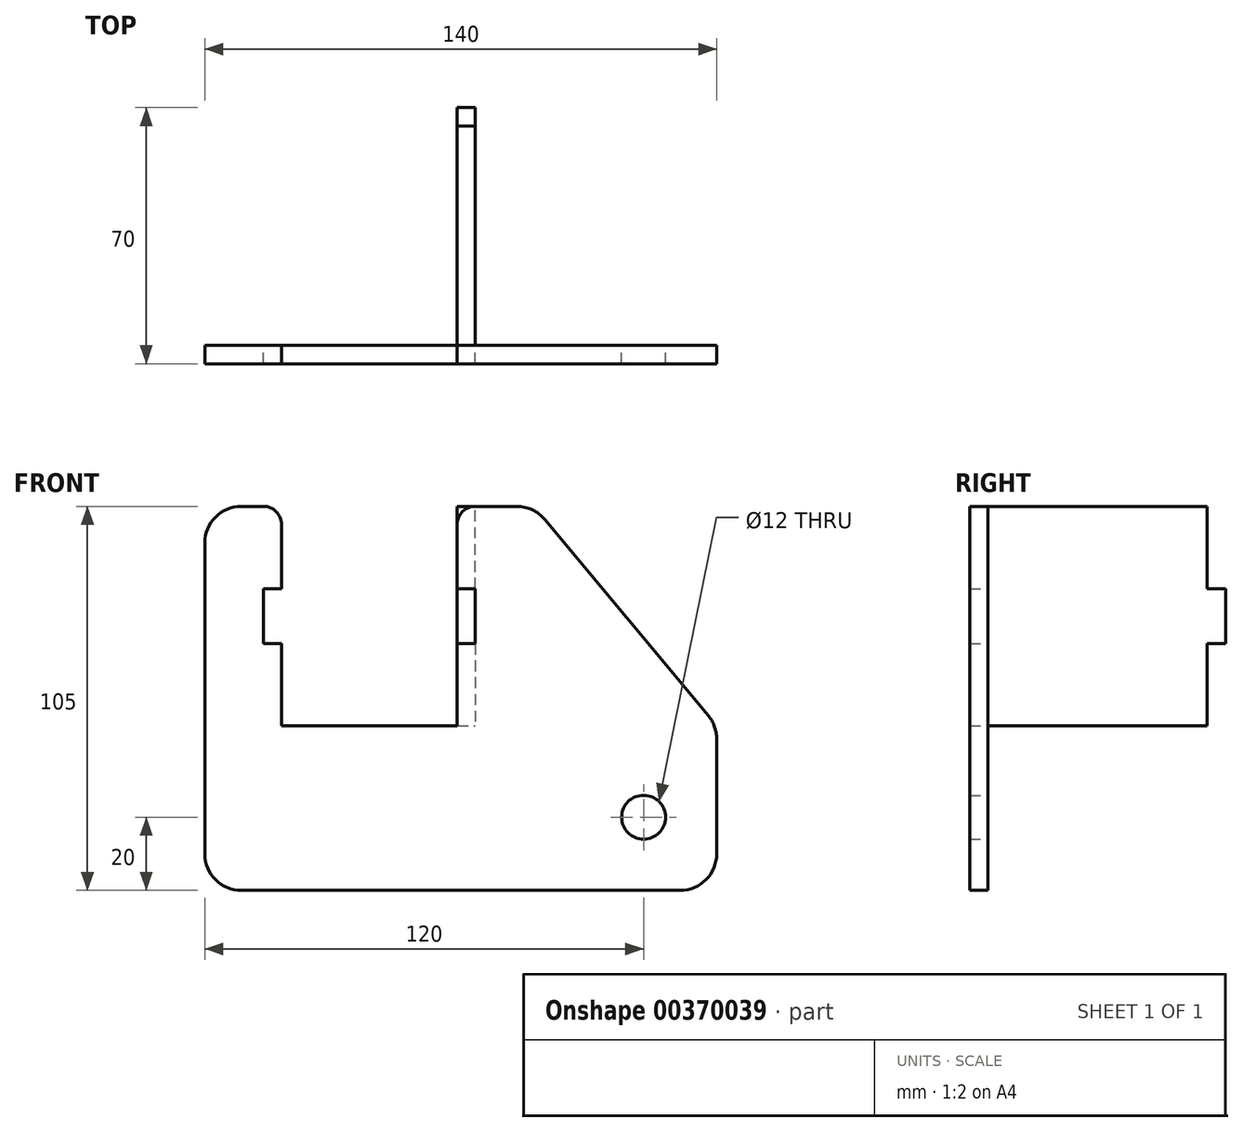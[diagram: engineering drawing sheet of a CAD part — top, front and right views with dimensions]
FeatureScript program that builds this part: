
annotation { "Feature Type Name" : "Feature", "Feature Type Description" : "" }
export const myFeature = defineFeature(function(context is Context, id is Id, definition is map)
    precondition{}
    {
        {
            var Q0;
            Q0=qCreatedBy(makeId("Front.planeOp"),FACE);
            var sketch = newSketch(context, id + "F0", { "sketchPlane" : qUnion([Q0])});
            skLineSegment(sketch, "E0", {"start": v(10, 0) * mm, "end": v(130, 0) * mm});
            skLineSegment(sketch, "E1", {"start": v(0, 10) * mm, "end": v(0, 95) * mm});
            skLineSegment(sketch, "E2", {"start": v(10, 105) * mm, "end": v(16, 105) * mm});
            skLineSegment(sketch, "E3", {"start": v(93, 101.4) * mm, "end": v(137.68, 47.78) * mm});
            skLineSegment(sketch, "E4", {"start": v(140, 41.38) * mm, "end": v(140, 10) * mm});
            skPoint(sketch, "E5", {"position": v(21, 45) * mm});
            skPoint(sketch, "E6", {"position": v(45, 105) * mm});
            skLineSegment(sketch, "E7", {"start": v(21, 45) * mm, "end": v(21, 100) * mm});
            skLineSegment(sketch, "E8", {"start": v(21, 45) * mm, "end": v(69, 45) * mm});
            skLineSegment(sketch, "E9", {"start": v(69, 45) * mm, "end": v(69, 100) * mm});
            skPoint(sketch, "E10", {"position": v(21, 75) * mm});
            skLineSegment(sketch, "E11", {"start": v(21, 75) * mm, "end": v(21, 82.5) * mm});
            skLineSegment(sketch, "E12", {"start": v(21, 82.5) * mm, "end": v(16, 82.5) * mm});
            skLineSegment(sketch, "E13", {"start": v(16, 82.5) * mm, "end": v(16, 67.5) * mm});
            skLineSegment(sketch, "E14", {"start": v(16, 67.5) * mm, "end": v(21, 67.5) * mm});
            skLineSegment(sketch, "E15", {"start": v(45, 105) * mm, "end": v(45, 45) * mm, "construction": true});
            skLineSegment(sketch, "E16.MirrorCS", {"start": v(69, 82.5) * mm, "end": v(74, 82.5) * mm});
            skLineSegment(sketch, "E17.MirrorCS", {"start": v(74, 82.5) * mm, "end": v(74, 67.5) * mm});
            skLineSegment(sketch, "E18.MirrorCS", {"start": v(74, 67.5) * mm, "end": v(69, 67.5) * mm});
            skPoint(sketch, "E19.visualSharp", {"position": v(90, 105) * mm});
            skArc(sketch, "E19.filletArc", {"start": v(93, 101.4) * mm, "mid": v(89.56, 104.06) * mm, "end": v(85.32, 105) * mm});
            skPoint(sketch, "E20.visualSharp", {"position": v(0, 105) * mm});
            skArc(sketch, "E20.filletArc", {"start": v(10, 105) * mm, "mid": v(2.93, 102.07) * mm, "end": v(0, 95) * mm});
            skPoint(sketch, "E21.visualSharp", {"position": v(0, 0) * mm});
            skArc(sketch, "E21.filletArc", {"start": v(0, 10) * mm, "mid": v(2.93, 2.93) * mm, "end": v(10, 0) * mm});
            skPoint(sketch, "E22.visualSharp", {"position": v(140, 0) * mm});
            skArc(sketch, "E22.filletArc", {"start": v(130, 0) * mm, "mid": v(137.07, 2.93) * mm, "end": v(140, 10) * mm});
            skPoint(sketch, "E23.visualSharp", {"position": v(140, 45) * mm});
            skArc(sketch, "E23.filletArc", {"start": v(140, 41.38) * mm, "mid": v(139.4, 44.78) * mm, "end": v(137.68, 47.78) * mm});
            skPoint(sketch, "E24", {"position": v(120, 20) * mm});
            skCircle(sketch, "E25", {"center": v(120, 20) * mm, "radius": 6 * mm});
            skLineSegment(sketch, "E26.trimOffspring", {"start": v(74, 105) * mm, "end": v(85.32, 105) * mm});
            skPoint(sketch, "E27.visualSharp", {"position": v(21, 105) * mm});
            skArc(sketch, "E27.filletArc", {"start": v(21, 100) * mm, "mid": v(19.54, 103.54) * mm, "end": v(16, 105) * mm});
            skPoint(sketch, "E28.visualSharp", {"position": v(69, 105) * mm});
            skArc(sketch, "E28.filletArc", {"start": v(74, 105) * mm, "mid": v(70.46, 103.54) * mm, "end": v(69, 100) * mm});
            skSolve(sketch);
        }
        {
            var Q0;
            Q0=makeQuery(id+"F0.imprint","IMPRINT",FACE,{"disambiguationData":[TD([[makeQuery(id+"F0.imprint","IMPRINT",EDGE,{"derivedFrom":sQuery(id+"F0.wireOp",EDGE,"E0")}),1.0]])]});
            extrude(context, id + "F1", {"entities" : qUnion([Q0]), "depth" : 5 * mm});
        }
        {
            var Q0;
            Q0=makeQuery(id+"F1.opExtrude","SWEPT_FACE",FACE,{"disambiguationData":[OSD([sQuery(id+"F0.wireOp",EDGE,"E17.MirrorCS")])]});
            var sketch = newSketch(context, id + "F2", { "sketchPlane" : qUnion([Q0])});
            skLineSegment(sketch, "E29.0", {"start": v(5, 82.5) * mm, "end": v(5, 67.5) * mm});
            skLineSegment(sketch, "E30.0.1", {"start": v(0, 82.5) * mm, "end": v(5, 82.5) * mm});
            skLineSegment(sketch, "E30.0.3", {"start": v(5, 82.5) * mm, "end": v(0, 82.5) * mm});
            skLineSegment(sketch, "E31.0", {"start": v(5, 67.5) * mm, "end": v(0, 67.5) * mm});
            skLineSegment(sketch, "E32", {"start": v(0, 82.5) * mm, "end": v(0, 105) * mm});
            skLineSegment(sketch, "E33", {"start": v(0, 105) * mm, "end": v(-60, 105) * mm});
            skLineSegment(sketch, "E34", {"start": v(-60, 105) * mm, "end": v(-60, 45) * mm});
            skLineSegment(sketch, "E35", {"start": v(-60, 45) * mm, "end": v(0, 45) * mm});
            skLineSegment(sketch, "E36", {"start": v(0, 45) * mm, "end": v(0, 67.5) * mm});
            skLineSegment(sketch, "E37", {"start": v(-30, 105) * mm, "end": v(-30, 45) * mm, "construction": true});
            skLineSegment(sketch, "E38.MirrorCS", {"start": v(-65, 82.5) * mm, "end": v(-65, 67.5) * mm});
            skLineSegment(sketch, "E39.MirrorCS", {"start": v(-65, 67.5) * mm, "end": v(-60, 67.5) * mm});
            skLineSegment(sketch, "E40.MirrorCS", {"start": v(-65, 82.5) * mm, "end": v(-60, 82.5) * mm});
            skSolve(sketch);
        }
        {
            var Q0;
            Q0 = qSketchRegion(id + "F2", true);
            extrude(context, id + "F3", {"entities" : qUnion([Q0]), "depth" : 5 * mm});
        }
    });
